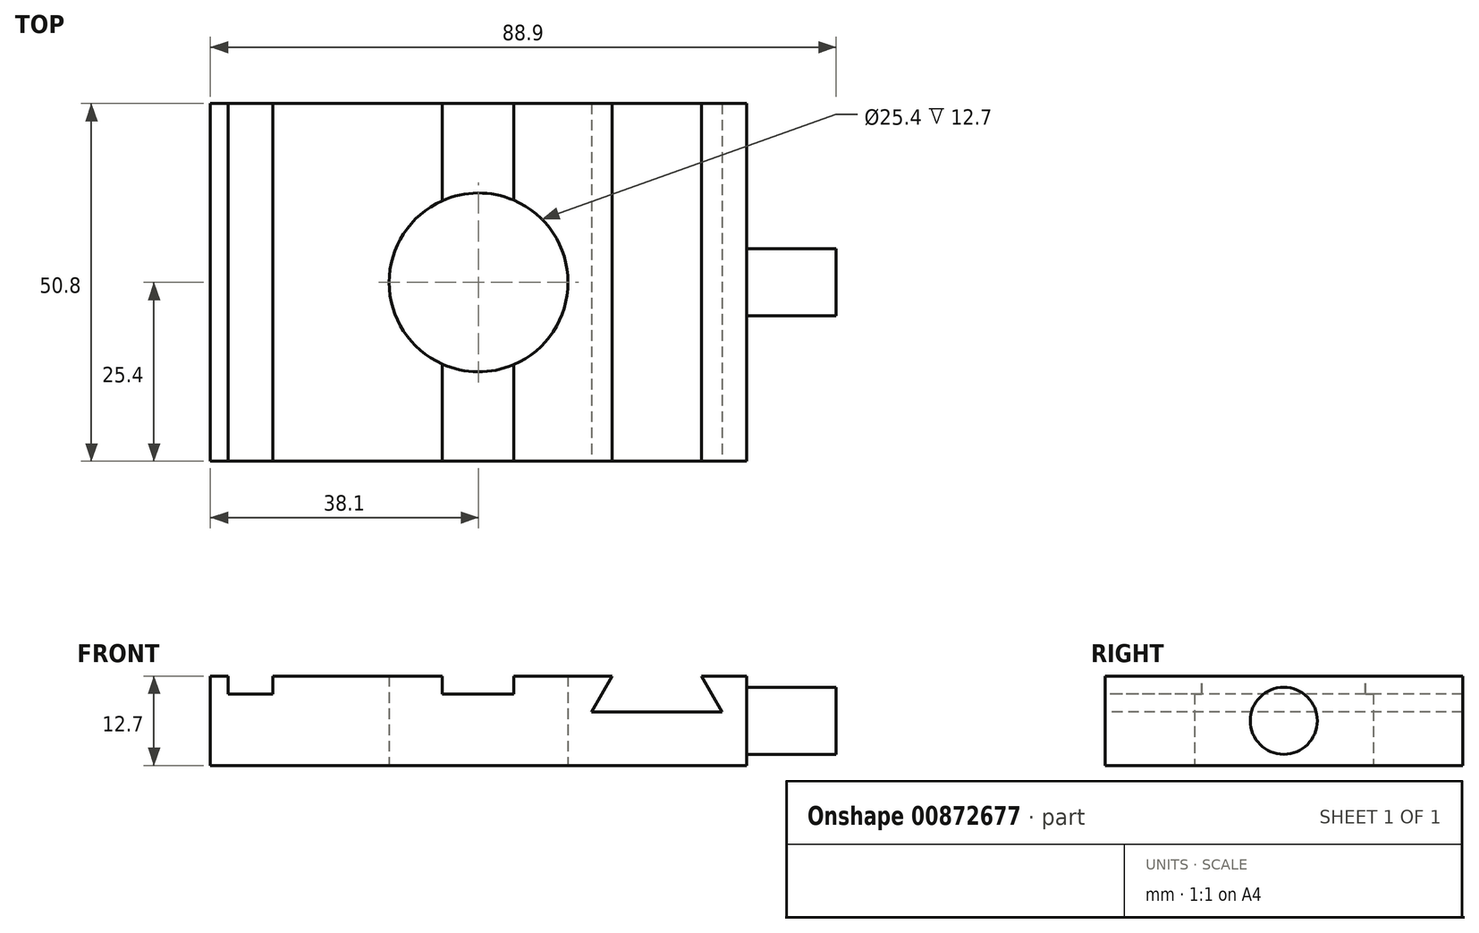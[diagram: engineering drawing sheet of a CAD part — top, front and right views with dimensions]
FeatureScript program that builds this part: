
annotation { "Feature Type Name" : "Feature", "Feature Type Description" : "" }
export const myFeature = defineFeature(function(context is Context, id is Id, definition is map)
    precondition{}
    {
        {
            var Q0;
            Q0=qCreatedBy(makeId("Top.planeOp"),FACE);
            var sketch = newSketch(context, id + "F0", { "sketchPlane" : qUnion([Q0])});
            skLineSegment(sketch, "E0.bottom", {"start": v(38.1, 25.4) * mm, "end": v(-38.1, 25.4) * mm});
            skLineSegment(sketch, "E0.top", {"start": v(38.1, -25.4) * mm, "end": v(-38.1, -25.4) * mm});
            skLineSegment(sketch, "E0.left", {"start": v(38.1, 25.4) * mm, "end": v(38.1, -25.4) * mm});
            skLineSegment(sketch, "E0.right", {"start": v(-38.1, 25.4) * mm, "end": v(-38.1, -25.4) * mm});
            skPoint(sketch, "E0.middle", {"position": v(0, 0) * mm});
            skCircle(sketch, "E1", {"center": v(0, 0) * mm, "radius": 12.7 * mm});
            skSolve(sketch);
        }
        {
            var Q0;
            Q0=makeQuery(id+"F0.imprint","IMPRINT",FACE,{"disambiguationData":[TD([[makeQuery(id+"F0.imprint","IMPRINT",EDGE,{"derivedFrom":sQuery(id+"F0.wireOp",EDGE,"E0.bottom")}),1.0]])]});
            extrude(context, id + "F1", {"entities" : qUnion([Q0]), "depth" : 12.7 * mm, "offsetDistance" : 25.4 * mm});
        }
        {
            var Q0;
            Q0=makeQuery(id+"F1.opExtrude","CAP_FACE",FACE,{"disambiguationData":[OSD([sQuery(id+"F0.wireOp",EDGE,"E0.bottom"),sQuery(id+"F0.wireOp",EDGE,"E0.top"),sQuery(id+"F0.wireOp",EDGE,"E0.left"),sQuery(id+"F0.wireOp",EDGE,"E0.right"),sQuery(id+"F0.wireOp",EDGE,"E1")])],"isStart":false});
            var sketch = newSketch(context, id + "F2", { "sketchPlane" : qUnion([Q0])});
            skLineSegment(sketch, "E2.bottom", {"start": v(-35.56, 25.4) * mm, "end": v(-29.2, 25.4) * mm});
            skLineSegment(sketch, "E2.top", {"start": v(-35.56, -25.4) * mm, "end": v(-29.2, -25.4) * mm});
            skLineSegment(sketch, "E2.left", {"start": v(-35.56, 25.4) * mm, "end": v(-35.56, -25.4) * mm});
            skLineSegment(sketch, "E2.right", {"start": v(-29.2, 25.4) * mm, "end": v(-29.2, -25.4) * mm});
            skLineSegment(sketch, "E3", {"start": v(-5.18, 25.4) * mm, "end": v(-5.18, -25.4) * mm});
            skLineSegment(sketch, "E4", {"start": v(4.98, 25.4) * mm, "end": v(4.98, -25.4) * mm});
            skPoint(sketch, "E5", {"position": v(0, 0) * mm});
            skLineSegment(sketch, "E6", {"start": v(0, 25.4) * mm, "end": v(0, -25.4) * mm, "construction": true});
            skSolve(sketch);
        }
        {
            var Q0;
            Q0=makeQuery(id+"F2.imprint","IMPRINT",FACE,{"disambiguationData":[TD([[makeQuery(id+"F2.imprint","IMPRINT",EDGE,{"derivedFrom":sQuery(id+"F2.wireOp",EDGE,"E2.bottom")}),1.0]])]});
            var Q1;
            {var subQ0=sQuery(id+"F2.wireOp",EDGE,"E3");var subQ1=makeQuery(id+"F1.opExtrude","CAP_EDGE",EDGE,{"disambiguationData":[OSD([sQuery(id+"F0.wireOp",EDGE,"E0.top")])],"isStart":false});var subQ2=makeQuery(id+"F2.imprint","INTERSECT",VERTEX,{"derivedFrom":[subQ1,subQ0]});Q1=makeQuery(id+"F2.imprint","IMPRINT",FACE,{"disambiguationData":[TD([[makeQuery(id+"F2.imprint","IMPRINT",EDGE,{"disambiguationData":[TD([[subQ2,1.0]])],"derivedFrom":subQ0}),1.0]])]});}
            var Q2;
            {var subQ0=sQuery(id+"F2.wireOp",EDGE,"E3");var subQ1=makeQuery(id+"F1.opExtrude","CAP_EDGE",EDGE,{"disambiguationData":[OSD([sQuery(id+"F0.wireOp",EDGE,"E0.bottom")])],"isStart":false});var subQ2=makeQuery(id+"F2.imprint","INTERSECT",VERTEX,{"derivedFrom":[subQ1,subQ0]});Q2=makeQuery(id+"F2.imprint","IMPRINT",FACE,{"disambiguationData":[TD([[makeQuery(id+"F2.imprint","IMPRINT",EDGE,{"disambiguationData":[TD([[subQ2,-1.0]])],"derivedFrom":subQ0}),1.0]])]});}
            extrude(context, id + "F3", {"entities" : qUnion([Q0, Q1, Q2]), "operationType" : NewBodyOperationType.REMOVE, "oppositeDirection" : true, "depth" : 2.54 * mm, "offsetDistance" : 25.4 * mm});
        }
        {
            var Q0;
            Q0=makeQuery(id+"F1.opExtrude","SWEPT_FACE",FACE,{"disambiguationData":[OSD([sQuery(id+"F0.wireOp",EDGE,"E0.top")])]});
            var sketch = newSketch(context, id + "F4", { "sketchPlane" : qUnion([Q0])});
            skLineSegment(sketch, "E7", {"start": v(18.95, 12.7) * mm, "end": v(16.02, 7.62) * mm});
            skLineSegment(sketch, "E8", {"start": v(16.02, 7.62) * mm, "end": v(34.58, 7.62) * mm});
            skLineSegment(sketch, "E9", {"start": v(34.58, 7.62) * mm, "end": v(31.65, 12.7) * mm});
            skLineSegment(sketch, "E10", {"start": v(31.65, 12.7) * mm, "end": v(18.95, 12.7) * mm});
            skLineSegment(sketch, "E11", {"start": v(25.3, 7.62) * mm, "end": v(25.3, 12.7) * mm, "construction": true});
            skSolve(sketch);
        }
        {
            var Q0;
            Q0=makeQuery(id+"F4.imprint","IMPRINT",FACE,{"disambiguationData":[TD([[makeQuery(id+"F4.imprint","IMPRINT",EDGE,{"derivedFrom":sQuery(id+"F4.wireOp",EDGE,"E7")}),1.0]])]});
            extrude(context, id + "F5", {"entities" : qUnion([Q0]), "operationType" : NewBodyOperationType.REMOVE, "endBound" : BoundingType.THROUGH_ALL, "oppositeDirection" : true, "depth" : 27.03 * mm, "offsetDistance" : 25.4 * mm});
        }
        {
            var Q0;
            Q0=makeQuery(id+"F1.opExtrude","SWEPT_FACE",FACE,{"disambiguationData":[OSD([sQuery(id+"F0.wireOp",EDGE,"E0.left")])]});
            var sketch = newSketch(context, id + "F6", { "sketchPlane" : qUnion([Q0])});
            skCircle(sketch, "E12", {"center": v(0, 6.35) * mm, "radius": 4.76 * mm});
            skPoint(sketch, "E12.centerSnap0", {"position": v(-25.4, 6.35) * mm});
            skPoint(sketch, "E12.centerSnap1", {"position": v(0, 12.7) * mm});
            skSolve(sketch);
        }
        {
            var Q0;
            Q0 = qSketchRegion(id + "F6", true);
            extrude(context, id + "F7", {"entities" : qUnion([Q0]), "operationType" : NewBodyOperationType.ADD, "depth" : 12.7 * mm, "offsetDistance" : 25.4 * mm});
        }
    });
